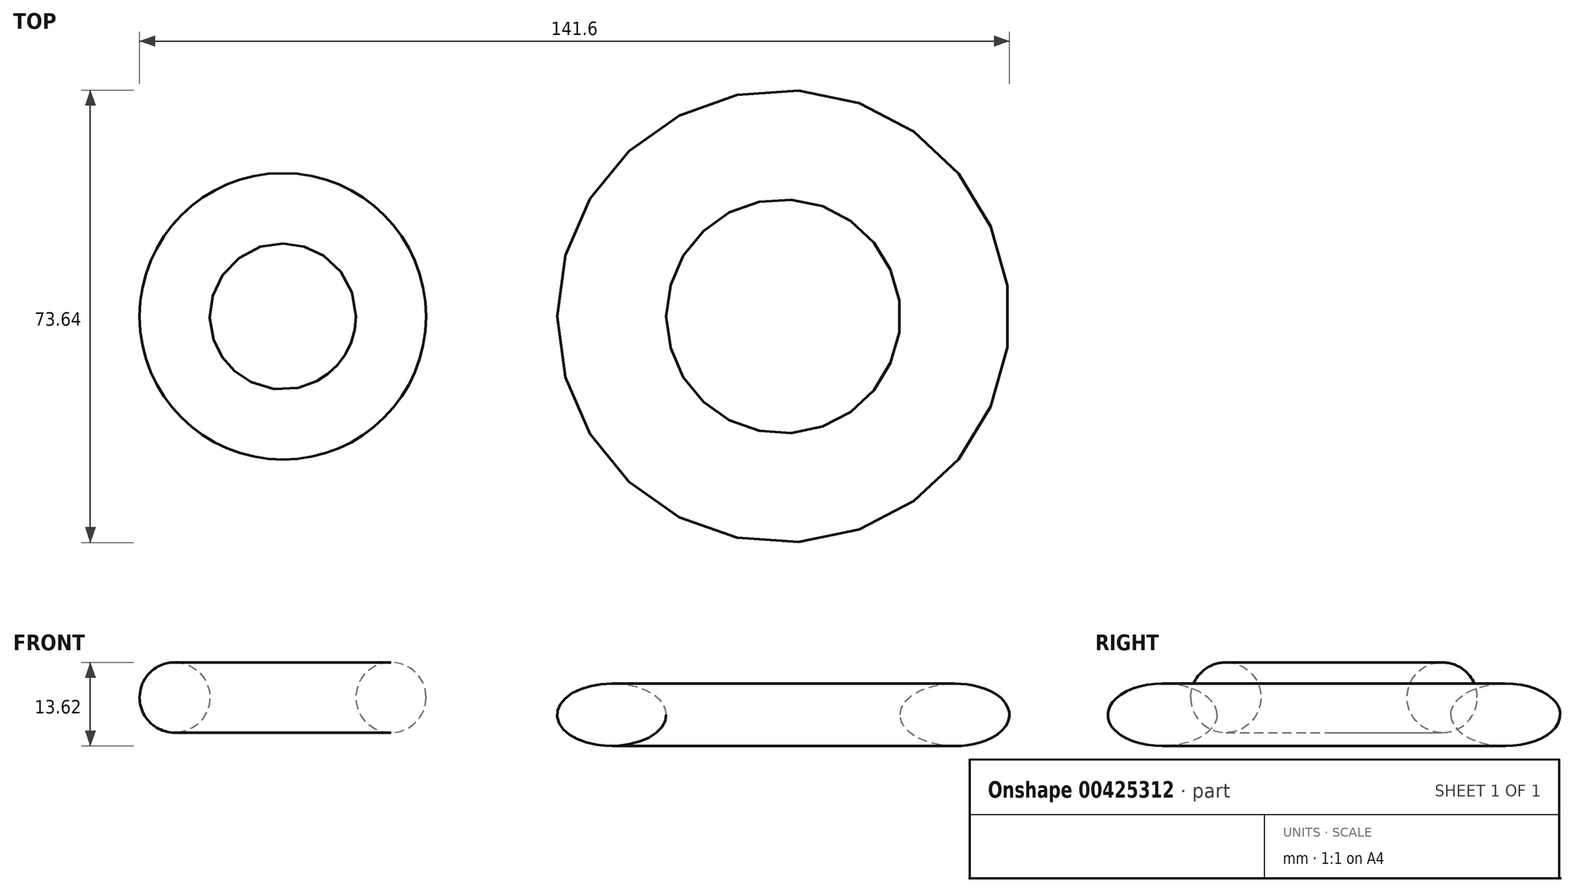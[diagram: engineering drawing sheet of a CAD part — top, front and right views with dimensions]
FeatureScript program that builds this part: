
annotation { "Feature Type Name" : "Feature", "Feature Type Description" : "" }
export const myFeature = defineFeature(function(context is Context, id is Id, definition is map)
    precondition{}
    {
        {
            var Q0;
            Q0=qCreatedBy(makeId("Front.planeOp"),FACE);
            var sketch = newSketch(context, id + "F0", { "sketchPlane" : qUnion([Q0])});
            skCircle(sketch, "E0", {"center": v(-46.3, 44.2) * mm, "radius": 5.72 * mm});
            skSolve(sketch);
        }
        {
            var Q0;
            Q0=qCreatedBy(makeId("Front.planeOp"),FACE);
            var sketch = newSketch(context, id + "F1", { "sketchPlane" : qUnion([Q0])});
            skLineSegment(sketch, "E1", {"start": v(-28.7, 57) * mm, "end": v(-28.7, 22.42) * mm});
            skSolve(sketch);
        }
        {
            var Q0;
            Q0=makeQuery(id+"F0.imprint","IMPRINT",FACE,{"disambiguationData":[TD([[makeQuery(id+"F0.imprint","IMPRINT",EDGE,{"derivedFrom":sQuery(id+"F0.wireOp",EDGE,"E0")}),1.0]])]});
            var Q1;
            Q1=sQuery(id+"F1.wireOp",EDGE,"E1");
            revolve(context, id + "F2", {"entities" : qUnion([Q0]), "axis" : qUnion([Q1]), "revolveType" : RevolveType.FULL});
        }
        {
            var Q0;
            Q0=qCreatedBy(makeId("Front.planeOp"),FACE);
            var sketch = newSketch(context, id + "F3", { "sketchPlane" : qUnion([Q0])});
            skEllipse(sketch, "E2", {"center": v(24.83, 41.38) * mm, "majorRadius": 8.9 * mm, "minorRadius": 5.08 * mm, "majorAxis": v(1, 0)});
            skSolve(sketch);
        }
        {
            var Q0;
            Q0=qCreatedBy(makeId("Front.planeOp"),FACE);
            var sketch = newSketch(context, id + "F4", { "sketchPlane" : qUnion([Q0])});
            skLineSegment(sketch, "E3", {"start": v(52.76, 57.12) * mm, "end": v(52.76, 51.5) * mm});
            skSolve(sketch);
        }
        {
            var Q0;
            Q0=makeQuery(id+"F3.imprint","IMPRINT",FACE,{"disambiguationData":[TD([[makeQuery(id+"F3.imprint","IMPRINT",EDGE,{"derivedFrom":sQuery(id+"F3.wireOp",EDGE,"E2")}),1.0]])]});
            var Q1;
            Q1=sQuery(id+"F4.wireOp",EDGE,"E3");
            revolve(context, id + "F5", {"entities" : qUnion([Q0]), "axis" : qUnion([Q1]), "revolveType" : RevolveType.FULL});
        }
    });
